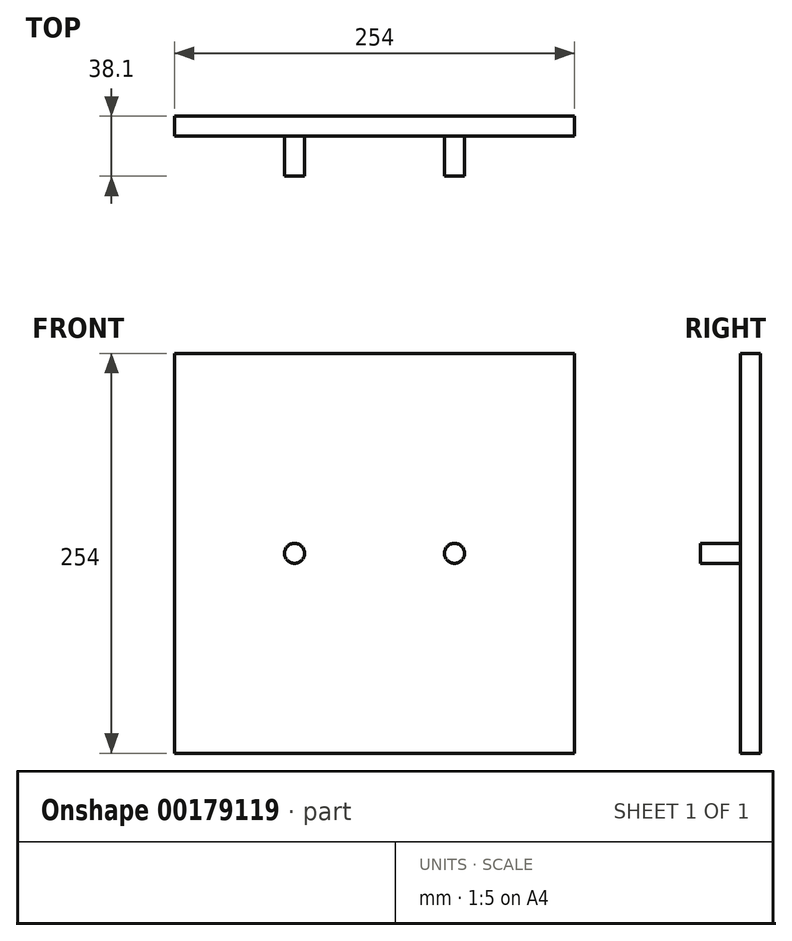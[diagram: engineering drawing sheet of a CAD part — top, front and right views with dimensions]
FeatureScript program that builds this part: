
annotation { "Feature Type Name" : "Feature", "Feature Type Description" : "" }
export const myFeature = defineFeature(function(context is Context, id is Id, definition is map)
    precondition{}
    {
        {
            var Q0;
            Q0=qCreatedBy(makeId("Front.planeOp"),FACE);
            var sketch = newSketch(context, id + "F0", { "sketchPlane" : qUnion([Q0])});
            skLineSegment(sketch, "E0.bottom", {"start": v(-127, 127) * mm, "end": v(127, 127) * mm});
            skLineSegment(sketch, "E0.top", {"start": v(-127, -127) * mm, "end": v(127, -127) * mm});
            skLineSegment(sketch, "E0.left", {"start": v(-127, 127) * mm, "end": v(-127, -127) * mm});
            skLineSegment(sketch, "E0.right", {"start": v(127, 127) * mm, "end": v(127, -127) * mm});
            skSolve(sketch);
        }
        {
            var Q0;
            Q0 = qSketchRegion(id + "F0", true);
            extrude(context, id + "F1", {"entities" : qUnion([Q0]), "depth" : 12.7 * mm});
        }
        {
            var Q0;
            Q0=makeQuery(id+"F1.opExtrude","CAP_FACE",FACE,{"disambiguationData":[OSD([sQuery(id+"F0.wireOp",EDGE,"E0.bottom"),sQuery(id+"F0.wireOp",EDGE,"E0.top"),sQuery(id+"F0.wireOp",EDGE,"E0.left"),sQuery(id+"F0.wireOp",EDGE,"E0.right")])],"isStart":false});
            var sketch = newSketch(context, id + "F2", { "sketchPlane" : qUnion([Q0])});
            skCircle(sketch, "E1", {"center": v(-50.8, 0) * mm, "radius": 6.35 * mm});
            skCircle(sketch, "E2", {"center": v(50.8, 0) * mm, "radius": 6.35 * mm});
            skSolve(sketch);
        }
        {
            var Q0;
            Q0 = qSketchRegion(id + "F2", true);
            extrude(context, id + "F3", {"entities" : qUnion([Q0]), "operationType" : NewBodyOperationType.ADD, "depth" : 25.4 * mm});
        }
    });
